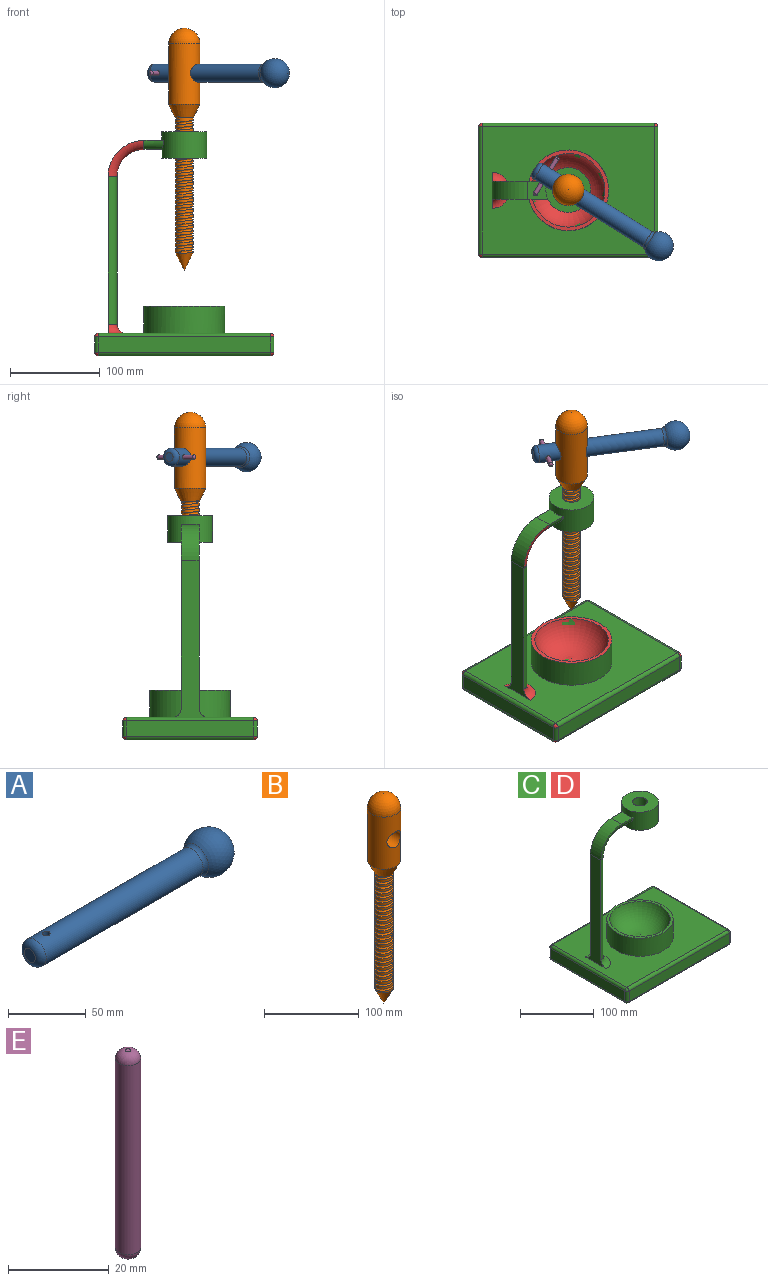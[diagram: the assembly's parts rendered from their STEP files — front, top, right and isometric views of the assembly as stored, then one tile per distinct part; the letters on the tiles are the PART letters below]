
ASSEMBLY  parts=5 mates=3
PART A: 6 faces, bbox 179.3x32.7x32.7 mm
  f0: plane 10x10mm, normal (-1,0,0), area 78.5mm2, adj f3
  f1: cylinder r=10mm len=142.74mm, axis (-1,0,0), area 8929.3mm2, adj f3,f4,f5
  f2: sphere r=16.34mm, area 2872.4mm2, adj f4
  f3: torus R=5mm, axis (1,0,0), area 403.8mm2, adj f0,f1
  f4: torus R=15mm, axis (1,0,0), area 261.2mm2, adj f1,f2
  f5: cylinder r=2.5mm len=20mm, axis (0,0,1), area 309.2mm2, adj f1
PART B: 9 faces, bbox 35.6x35.6x270.6 mm
  f0: cylinder r=10mm len=150mm, axis (0,0,-1), area 4649.9mm2, adj f1,f2,f5,f6,f7
  f1: cone r=17.5mm half-angle=26.4deg, axis (0,0,1), area 1445.9mm2, adj f0,f3,f6,f7
  f2: cone r=0mm half-angle=26.6deg, axis (0,0,1), area 691.7mm2, adj f0,f5,f7
  f3: cylinder r=17.5mm len=67.39mm, axis (0,0,-1), area 6754.2mm2, adj f1,f4,f8
  f4: sphere r=17.5mm, area 1924.2mm2, adj f3
  f5: plane 3.24x1.94mm, normal (0,1,0), area 2.8mm2, adj f0,f2,f7
  f6: plane 3.49x2.68mm, normal (0,-1,0), area 3.8mm2, adj f0,f1,f7
  f7: bspline ~155.8x26.44mm, area 6509.5mm2, adj f0,f1,f2,f5,f6
  f8: cylinder r=10mm len=35mm, axis (0,-1,0), area 2006.8mm2, adj f3
PART C: 45 faces, bbox 200x150x251 mm
  f0: plane 192x142mm, normal (0,0,-1), area 2289mm2, adj f20,f21,f22,f23,f25,f29,f30,f31
  f1: plane 192x142mm, normal (0,0,1), area 20274mm2, adj f6,f12,f15,f33,f38,f41,f44
  f2: plane 142x17mm, normal (-1,0,0), area 2414mm2, adj f30,f39,f40,f44
  f3: plane 142x17mm, normal (1,0,0), area 2414mm2, adj f25,f28,f32,f33
  f4: plane 192x17mm, normal (0,-1,0), area 3264mm2, adj f28,f29,f38,f39
  f5: plane 192x17mm, normal (0,1,0), area 3264mm2, adj f31,f32,f40,f41
  f6: plane 175x40mm, normal (-1,0,0), area 3542.9mm2, adj f1,f8,f15,f16
  f7: plane 22.09x20mm, normal (0,0,1), area 413.7mm2, adj f8,f10,f18
  f8: cylinder r=40mm len=40mm, axis (0,1,0), area 1256.6mm2, adj f6,f7,f17
  f9: plane 50x50mm, normal (0,0,-1), area 1649.3mm2, adj f10,f19
  f10: cylinder r=25mm len=50mm, axis (0,0,1), area 4552mm2, adj f7,f9,f11,f18
  f11: plane 50x50mm, normal (0,0,1), area 1649.3mm2, adj f10,f19
  f12: cylinder r=45mm len=90mm, axis (0,0,-1), area 8482.3mm2, adj f1,f13
  f13: plane 90x90mm, normal (0,0,1), area 1080.7mm2, adj f12,f14
  f14: torus R=6.26mm, axis (0,0,-1), area 7977.6mm2, adj f13
  f15: torus R=20mm, axis (0,0,1), area 672.8mm2, adj f1,f6,f16
  f16: cylinder r=10mm len=165mm, axis (0,0,-1), area 5183.6mm2, adj f6,f15,f17
  f17: torus R=40mm, axis (0,-1,0), area 1659.8mm2, adj f8,f16,f18
  f18: cylinder r=10mm len=22.09mm, axis (-1,0,0), area 660.7mm2, adj f7,f10,f17
  f19: cylinder r=10mm len=30mm, axis (0,0,-1), area 1885mm2, adj f9,f11
  f20: plane 135x15mm, normal (-1,0,0), area 2025mm2, adj f0,f21,f23,f24
  f21: plane 185x15mm, normal (0,1,0), area 2775mm2, adj f0,f20,f22,f24
  f22: plane 135x15mm, normal (1,0,0), area 2025mm2, adj f0,f21,f23,f24
  f23: plane 185x15mm, normal (0,-1,0), area 2775mm2, adj f0,f20,f22,f24
  f24: plane 185x135mm, normal (0,0,-1), area 24975mm2, adj f20,f21,f22,f23
  f25: cylinder r=4mm len=142mm, axis (0,-1,0), area 892.2mm2, adj f0,f3,f26,f27
  f26: sphere r=4mm, area 25.1mm2, adj f25,f28,f29
  f27: sphere r=4mm, area 25.1mm2, adj f25,f31,f32
  f28: cylinder r=4mm len=17mm, axis (0,0,-1), area 106.8mm2, adj f3,f4,f26,f34
  f29: cylinder r=4mm len=192mm, axis (-1,0,0), area 1206.4mm2, adj f0,f4,f26,f35
  f30: cylinder r=4mm len=142mm, axis (0,1,0), area 892.2mm2, adj f0,f2,f35,f36
  f31: cylinder r=4mm len=192mm, axis (1,0,0), area 1206.4mm2, adj f0,f5,f27,f36
  f32: cylinder r=4mm len=17mm, axis (0,0,1), area 106.8mm2, adj f3,f5,f27,f37
  f33: cylinder r=4mm len=142mm, axis (0,1,0), area 892.2mm2, adj f1,f3,f34,f37
  f34: sphere r=4mm, area 25.1mm2, adj f28,f33,f38
  f35: sphere r=4mm, area 25.1mm2, adj f29,f30,f39
  f36: sphere r=4mm, area 25.1mm2, adj f30,f31,f40
  f37: sphere r=4mm, area 25.1mm2, adj f32,f33,f41
  f38: cylinder r=4mm len=192mm, axis (1,0,0), area 1206.4mm2, adj f1,f4,f34,f42
  f39: cylinder r=4mm len=17mm, axis (0,0,1), area 106.8mm2, adj f2,f4,f35,f42
  f40: cylinder r=4mm len=17mm, axis (0,0,-1), area 106.8mm2, adj f2,f5,f36,f43
  f41: cylinder r=4mm len=192mm, axis (-1,0,0), area 1206.4mm2, adj f1,f5,f37,f43
  f42: sphere r=4mm, area 25.1mm2, adj f38,f39,f44
  f43: sphere r=4mm, area 25.1mm2, adj f40,f41,f44
  f44: cylinder r=4mm len=142mm, axis (0,-1,0), area 892.2mm2, adj f1,f2,f42,f43
PART D: same geometry as C
PART E: 5 faces, bbox 5x5x50 mm
  f0: cylinder r=2.5mm len=46mm, axis (0,0,-1), area 722.6mm2, adj f3,f4
  f1: plane 1x1mm, normal (0,0,1), area 0.8mm2, adj f3
  f2: plane 1x1mm, normal (0,0,-1), area 0.8mm2, adj f4
  f3: torus R=0.5mm, axis (0,0,1), area 35mm2, adj f0,f1
  f4: torus R=0.5mm, axis (0,0,1), area 35mm2, adj f0,f2
PLACE A rot(axis=(-0.93,0.26,-0.26),94.3deg) t=(-16.76,-52.72,228.99)mm
PLACE B rot(axis=(0,0,-1),121.9deg) t=(-43.01,-36.4,28.99)mm
PLACE C t=(-43.01,-36.4,-61.13)mm
PLACE D t=(-43.01,-36.4,-61.13)mm fixed
PLACE E rot(axis=(0.66,0.37,-0.66),139.8deg) t=(-67.71,-21.04,228.99)mm
MATE fastened E.f0 <-> A.f5  axis (0.53,0.85,0) through (-67.71,-21.04,228.99)mm
MATE slider A.f3 <-> B.f8  axis (-0.85,0.53,0) through (-15.59,-53.45,228.99)mm
MATE cylindrical B.f0 <-> D.f19  axis (0,0,-1) through (-43.01,-36.4,28.99)mm
